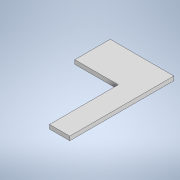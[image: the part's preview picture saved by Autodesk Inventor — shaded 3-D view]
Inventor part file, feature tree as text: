
AUTODESK INVENTOR PART (.ipt)
format: ipt  version: 2020 (Build 240168000, 168)  size: 97,280 bytes
history: native  units: mm
features: other x1, extrude x1, sketch x1
ambient origin geometry x8: Origin, YZ Plane, XZ Plane, XY Plane, X Axis, Y Axis, Z Axis, Center Point
bodies: Body1 (feature_tree)
feature tree (3):
  other  "Bryła1"
  extrude  "Wyciągnięcie proste1"  Depth=63.0mm
  sketch  "Szkic1"
